# Revit family: BOS-Oberlichtzarge-Rb4r15ZBsd_Familie
name_source: partatom
category: Türen
revit_build: Autodesk Revit 2017 (Build: 20160225_1515(x64)
units: mm (PartAtom-declared; Revit-internal decimal feet)

## family parameters
Basisbauteil = Wand
Beim Laden mit Abzugskörper schneiden = Nein
Gemeinsam genutzt = Nein
Immer vertikal = Ja
Raumberechnungspunkt = Ja

## types (2) — shared parameters
Aluminiumglasleistenbreite = 12 mm  [stored 0.0393701 ft]
Aluminiumglasleistenhöhe = 15 mm  [stored 0.0492126 ft]
Ankerabstand vorne = 21.5 mm  [stored 0.0705381 ft]
BBL1 Bandbezugslinie   Hinge Position 1 = 241 mm  [stored 0.790682 ft]
BE max. = 100 mm  [stored 0.328084 ft]
Bauelement = BOS Stahlzarge
Blechstärke = 2 mm  [stored 0.00656168 ft]
Dichtung 1 = Ja
Drehpunkt Warnung sichtbar = Ja
Drehpunktabstand (FM) horizontal = 17.5 mm  [stored 0.0574147 ft]
Drehpunktabstand (PV) vertikal = -17.5 mm  [stored -0.0574147 ft]
Drehpunktreferenz = 500 mm  [stored 1.64042 ft]
Einfügepunkt = 17 mm
FMB max. = 1341 mm  [stored 4.39961 ft]
FMB min. = 591 mm  [stored 1.93898 ft]
FMH2 max. = 2483 mm  [stored 8.14633 ft]
FMH2 min. = 1608 mm  [stored 5.27559 ft]
FMH3 max. = 1000 mm  [stored 3.28084 ft]
FMH3 min. = 100 mm  [stored 0.328084 ft]
Falzaufschlag = 15 mm  [stored 0.0492126 ft]
Falztiefe = 67.5 mm  [stored 0.221457 ft]
Falztiefe 2 = 25 mm  [stored 0.082021 ft]
Funktion = Innen
GT max. = 650 mm  [stored 2.13255 ft]
Gefälzt = Nein
Hersteller = BOS GmbH Best Of Steel, Lütkenfelde 4, D-48282 Emsdetten
Info-Texte sichtbar = Ja
Information in English = Nein
Leibungstiefe Kämpfer max. = 40 mm  [stored 0.131234 ft]
Leibungstiefe Kämpfer min. = 40 mm  [stored 0.131234 ft]
MW min. = 100 mm  [stored 0.328084 ft]
Material = grundiert, feuerverzinktes Feinblech nach DIN EN 10143
Material - Bänder = <Nach Kategorie>
Material - Dichtung = <Nach Kategorie>
Material - Drückergarnitur = <Nach Kategorie>
Material - Eckabdeckung = <Nach Kategorie>
Material - Glasleisten = <Nach Kategorie>
Material - Schließblech = <Nach Kategorie>
Material - Türblatt = <Nach Kategorie>
Material - Verglasung = Glas
Material - Vorlegeband = <Nach Kategorie>
Material - Zarge = <Nach Kategorie>
Putzwinkel max. = 30 mm  [stored 0.0984252 ft]
Putzwinkel min. = 30 mm  [stored 0.0984252 ft]
Radius innen = 15.5 mm  [stored 0.050853 ft]
Sickentiefe = 10 mm  [stored 0.0328084 ft]
Spiegel vorne max. = 35 mm  [stored 0.114829 ft]
Spiegel vorne min. = 35 mm  [stored 0.114829 ft]
Stumpf = Ja
Technische Infos rund um die Stahlzarge = www.BestOfSteel.de/tools-downloads/technische-infos-rund-um-die-stahlzarge/
Türblattabstand 1 = -17 mm
Türblattabstand 2 = 10.5 mm  [stored 0.0344488 ft]
Türblattabstand 3 = 10.5 mm  [stored 0.0344488 ft]
Türblattabstand links-rechts = 3.5 mm  [stored 0.0114829 ft]
Türblattabstand oben = 4 mm  [stored 0.0131234 ft]
Türblattabstand unten = 7 mm  [stored 0.0229659 ft]
Türblattaufschlag = 13 mm
Türblattstärke 2 = 40 mm  [stored 0.131234 ft]
Türblattversatz horizontal = 21 mm  [stored 0.0688976 ft]
Türblattversatz vertikal = -0.5 mm  [stored -0.00164042 ft]
URL = www.BestOfSteel.de/stahlzargen/zargen-fuer-drehfluegeltueren/elementzargen/oberlichtzargen/
Unterfütterungsstärke = 5 mm  [stored 0.0164042 ft]
Öffnungswinkel max. = 180.00°
Öffnungswinkel min. = 0.00°
zero-valued in all types: Breite, Dicke, Rohbaubreite, Rohbauhöhe, Spiegelversatz vorne Kämpfer, Türblattstärke 1

## per-type parameters (varying)
| type | Beschreibung | Dichtung 1 Oberlicht | Dichtung 2 | Doppelfalz | Einfachfalz | Falzaufschlag gesamt | Falztiefe gesamt | Glasabstand umlaufend | Rb4r15ZBsFd/KEsFd | Rb4r15ZBsd/KEsd | Rohrglasleistenbreite | Rohrglasleistenhöhe | Rohrglasleistenprofilverschiebung horizontal | Rohrglasleistenprofilverschiebung vertikal | Spiegel hinten max. | Spiegel hinten min. | Türblattstärke | Türblattstärke 3 |
| Rb4r15ZBsd/KEsd | 2-schalige Oberlichtzarge als SafetyDesign, stumpf | Ja | Nein | Nein | Ja | 15 mm  [stored 0.0492126 ft] | 67.5 mm  [stored 0.221457 ft] | 5 mm  [stored 0.0164042 ft] | Nein | Ja | 10 mm  [stored 0.0328084 ft] | 15 mm  [stored 0.0492126 ft] | 7.5 mm  [stored 0.0246063 ft] | -5 mm  [stored -0.0164042 ft] | 50 mm  [stored 0.164042 ft] | 50 mm  [stored 0.164042 ft] | 40 mm  [stored 0.131234 ft] | 0 mm  [stored 0 ft] |
| Rb4r15ZBsFd/KEsFd | 2-schalige Oberlichtzarge als SafetyDesign, stumpf, mit Doppelfalz | Nein | Ja | Ja | Nein | 30 mm  [stored 0.0984252 ft] | 92.5 mm  [stored 0.303478 ft] | 20 mm  [stored 0.0656168 ft] | Ja | Nein | 15 mm  [stored 0.0492126 ft] | 30 mm  [stored 0.0984252 ft] | 15 mm  [stored 0.0492126 ft] | -7.5 mm  [stored -0.0246063 ft] | 65 mm  [stored 0.213255 ft] | 65 mm  [stored 0.213255 ft] | 65 mm  [stored 0.213255 ft] | 25 mm  [stored 0.082021 ft] |

note: column(s) folded — value = type name in every type: Modell

note: [stored X ft] marks values corroborated as IEEE doubles in the binary element streams (Revit-internal decimal feet)
